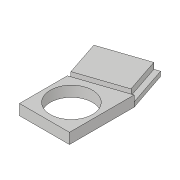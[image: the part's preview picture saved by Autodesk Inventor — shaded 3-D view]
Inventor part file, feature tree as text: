
AUTODESK INVENTOR PART (.ipt)
format: ipt  version: 2018.3 (Build 223284000, 284)  size: 116,736 bytes
history: native  units: in
note: dims shown in document units (in); Inventor stores cm internally (conversion verified against a paired STEP export)
features: extrude x3, sketch x3
ambient origin geometry x8: Origin, YZ Plane, XZ Plane, XY Plane, X Axis, Y Axis, Z Axis, Center Point
bodies: Solid1 (feature_tree)
feature tree (6):
  extrude  "Extrusion1"  Depth=0.119in
  extrude  "Extrusion2"  Depth=0.1105in
  extrude  "Extrusion3"  Depth=0.125in
  sketch  "Sketch1"  dims[d1=0.875in d2=1.1003in d3=1.0432in d4=0.88in d5=0.221in d6=0.0in d11=0.119in]
  sketch  "Sketch2"  dims[d13=0.125in d14=0.0in d17=0.1105in]
  sketch  "Sketch3"  dims[d18=0.125in d19=0.0in d20=0.5625in d23=1.0in]
